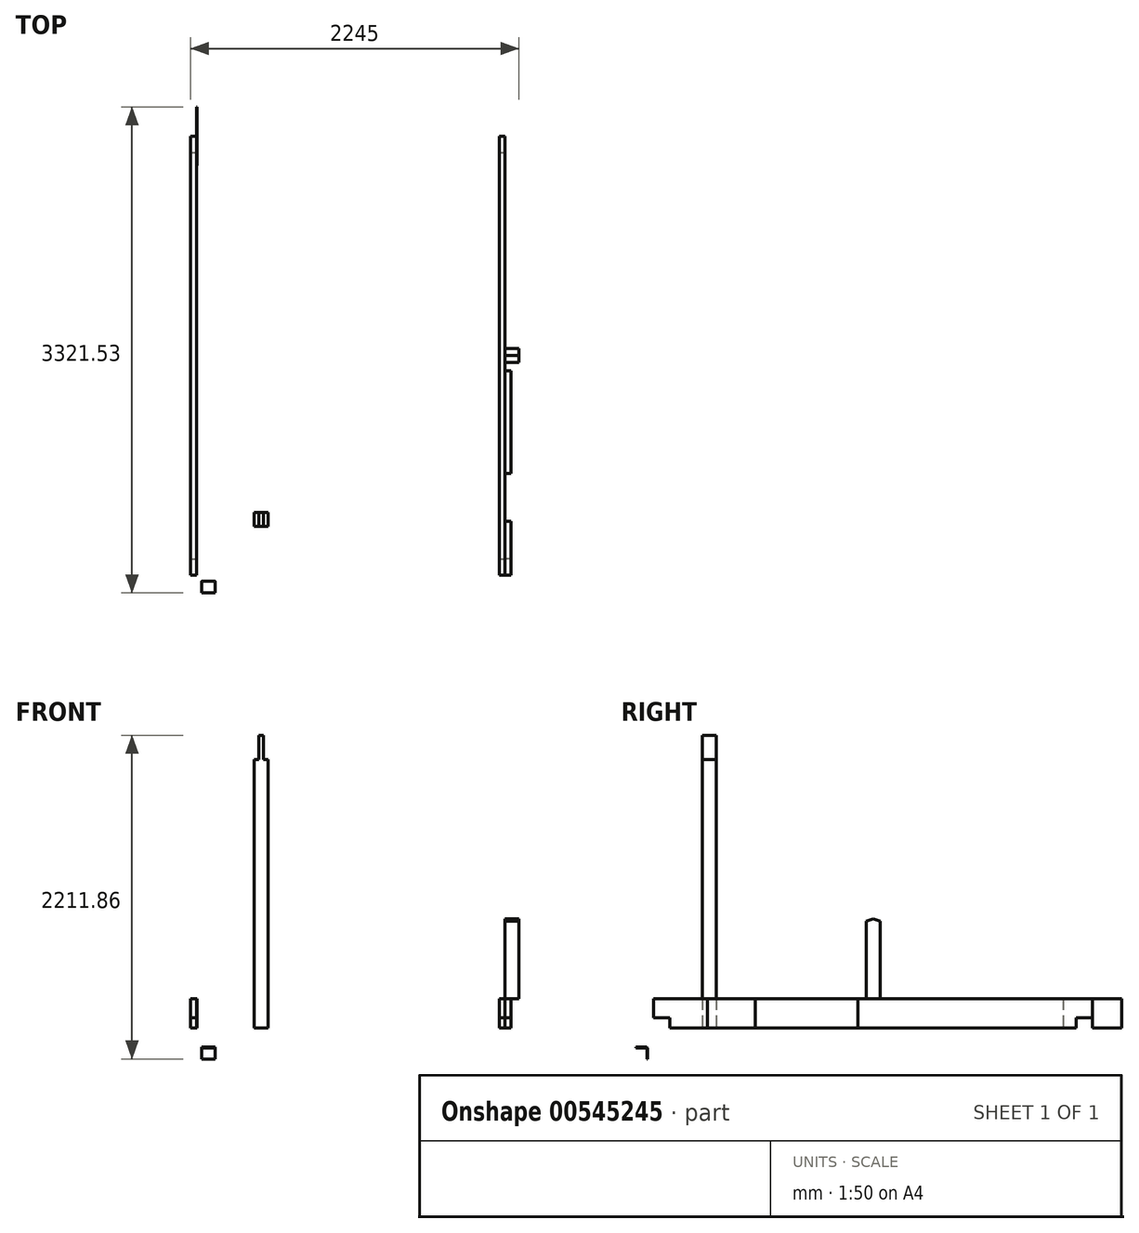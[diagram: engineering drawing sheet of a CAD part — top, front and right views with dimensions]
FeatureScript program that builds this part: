
annotation { "Feature Type Name" : "Feature", "Feature Type Description" : "" }
export const myFeature = defineFeature(function(context is Context, id is Id, definition is map)
    precondition{}
    {
        {
            assignVariable(context, id + "F0", {"name" : "dBalken", "anyValue" : 95});
        }
        {
            assignVariable(context, id + "F1", {"name" : "dBohle", "anyValue" : 40});
        }
        {
            var Q0;
            Q0=qCreatedBy(makeId("Top.planeOp"),FACE);
            var sketch = newSketch(context, id + "F2", { "sketchPlane" : qUnion([Q0])});
            skLineSegment(sketch, "E0.bottom", {"start": v(-76.6, 2841.51) * mm, "end": v(-36.6, 2841.51) * mm});
            skLineSegment(sketch, "E0.top", {"start": v(-76.6, -158.49) * mm, "end": v(-36.6, -158.49) * mm});
            skLineSegment(sketch, "E0.left", {"start": v(-76.6, 2841.51) * mm, "end": v(-76.6, -158.49) * mm});
            skLineSegment(sketch, "E0.right", {"start": v(-36.6, 2841.51) * mm, "end": v(-36.6, -158.49) * mm});
            skLineSegment(sketch, "E1.bottom", {"start": v(357.98, 268.38) * mm, "end": v(452.98, 268.38) * mm});
            skLineSegment(sketch, "E1.top", {"start": v(357.98, 173.38) * mm, "end": v(452.98, 173.38) * mm});
            skLineSegment(sketch, "E1.left", {"start": v(357.98, 268.38) * mm, "end": v(357.98, 173.38) * mm});
            skLineSegment(sketch, "E1.right", {"start": v(452.98, 268.38) * mm, "end": v(452.98, 173.38) * mm});
            skSolve(sketch);
        }
        {
            var Q0;
            Q0=makeQuery(id+"F2.imprint","IMPRINT",FACE,{"disambiguationData":[TD([[makeQuery(id+"F2.imprint","IMPRINT",EDGE,{"derivedFrom":sQuery(id+"F2.wireOp",EDGE,"E0.bottom")}),-1.0]])]});
            extrude(context, id + "F3", {"entities" : qUnion([Q0]), "depth" : 200 * mm, "offsetDistance" : 25 * mm});
        }
        {
            var Q0;
            Q0=makeQuery(id+"F2.imprint","IMPRINT",FACE,{"disambiguationData":[TD([[makeQuery(id+"F2.imprint","IMPRINT",EDGE,{"derivedFrom":sQuery(id+"F2.wireOp",EDGE,"E1.bottom")}),-1.0]])]});
            extrude(context, id + "F4", {"entities" : qUnion([Q0]), "depth" : 2000 * mm, "offsetDistance" : 25 * mm});
        }
        {
            var Q0;
            Q0=makeQuery(id+"F4.opExtrude","SWEPT_FACE",FACE,{"disambiguationData":[OSD([sQuery(id+"F2.wireOp",EDGE,"E1.top")])]});
            var sketch = newSketch(context, id + "F5", { "sketchPlane" : qUnion([Q0])});
            skLineSegment(sketch, "E2", {"start": v(405.48, 2000) * mm, "end": v(405.48, 2049.78) * mm, "construction": true});
            skLineSegment(sketch, "E3", {"start": v(389.98, 2000) * mm, "end": v(389.98, 1835.86) * mm});
            skLineSegment(sketch, "E4", {"start": v(389.98, 1835.86) * mm, "end": v(357.98, 1835.86) * mm});
            skLineSegment(sketch, "E5.MirrorCS", {"start": v(420.98, 2000) * mm, "end": v(420.98, 1835.86) * mm});
            skLineSegment(sketch, "E6.MirrorCS", {"start": v(420.98, 1835.86) * mm, "end": v(452.98, 1835.86) * mm});
            skSolve(sketch);
        }
        {
            var Q0;
            {var subQ0=sQuery(id+"F5.wireOp",EDGE,"E3");Q0=makeQuery(id+"F5.imprint","IMPRINT",FACE,{"disambiguationData":[TD([[makeQuery(id+"F5.imprint","IMPRINT",EDGE,{"derivedFrom":subQ0}),-1.0]])]});}
            var Q1;
            {var subQ0=sQuery(id+"F5.wireOp",EDGE,"E5.MirrorCS");Q1=makeQuery(id+"F5.imprint","IMPRINT",FACE,{"disambiguationData":[TD([[makeQuery(id+"F5.imprint","IMPRINT",EDGE,{"derivedFrom":subQ0}),1.0]])]});}
            extrude(context, id + "F6", {"entities" : qUnion([Q0, Q1]), "operationType" : NewBodyOperationType.REMOVE, "endBound" : BoundingType.THROUGH_ALL, "oppositeDirection" : true, "depth" : 25 * mm, "offsetDistance" : 25 * mm});
        }
        {
            var Q0;
            Q0=qCreatedBy(makeId("Right.planeOp"),FACE);
            var sketch = newSketch(context, id + "F7", { "sketchPlane" : qUnion([Q0])});
            skLineSegment(sketch, "E7", {"start": v(-280.02, -131.86) * mm, "end": v(-210.02, -131.86) * mm});
            skLineSegment(sketch, "E8", {"start": v(-200.02, -211.86) * mm, "end": v(-200.02, -141.86) * mm});
            skLineSegment(sketch, "E9.0", {"start": v(-205.02, -211.86) * mm, "end": v(-205.02, -141.86) * mm});
            skLineSegment(sketch, "E9.1", {"start": v(-280.02, -136.86) * mm, "end": v(-210.02, -136.86) * mm});
            skLineSegment(sketch, "E10", {"start": v(-280.02, -131.86) * mm, "end": v(-280.02, -136.86) * mm});
            skLineSegment(sketch, "E11", {"start": v(-205.02, -211.86) * mm, "end": v(-200.02, -211.86) * mm});
            skPoint(sketch, "E12.visualSharp", {"position": v(-205.02, -136.86) * mm});
            skArc(sketch, "E12.filletArc", {"start": v(-205.02, -141.86) * mm, "mid": v(-206.48, -138.32) * mm, "end": v(-210.02, -136.86) * mm});
            skPoint(sketch, "E13.visualSharp", {"position": v(-200.02, -131.86) * mm});
            skArc(sketch, "E13.filletArc", {"start": v(-200.02, -141.86) * mm, "mid": v(-202.95, -134.78) * mm, "end": v(-210.02, -131.86) * mm});
            skSolve(sketch);
        }
        {
            var Q0;
            Q0=makeQuery(id+"F7.imprint","IMPRINT",FACE,{"disambiguationData":[TD([[makeQuery(id+"F7.imprint","IMPRINT",EDGE,{"derivedFrom":sQuery(id+"F7.wireOp",EDGE,"E7")}),-1.0]])]});
            extrude(context, id + "F8", {"entities" : qUnion([Q0]), "depth" : 90 * mm, "offsetDistance" : 25 * mm});
        }
        {
            var Q0;
            Q0=makeQuery(id+"F3.opExtrude","SWEPT_FACE",FACE,{"disambiguationData":[OSD([sQuery(id+"F2.wireOp",EDGE,"E0.right")])]});
            var sketch = newSketch(context, id + "F9", { "sketchPlane" : qUnion([Q0])});
            skLineSegment(sketch, "E14.0", {"start": v(2841.51, 200) * mm, "end": v(-158.49, 200) * mm, "construction": true});
            skLineSegment(sketch, "E15.0", {"start": v(2841.51, 200) * mm, "end": v(2841.51, 0) * mm, "construction": true});
            skLineSegment(sketch, "E16.0", {"start": v(2841.51, 0) * mm, "end": v(-158.49, 0) * mm, "construction": true});
            skLineSegment(sketch, "E17.bottom", {"start": v(2641.51, 200) * mm, "end": v(2841.51, 200) * mm});
            skLineSegment(sketch, "E17.top", {"start": v(2641.51, 0) * mm, "end": v(2841.51, 0) * mm});
            skLineSegment(sketch, "E17.left", {"start": v(2641.51, 200) * mm, "end": v(2641.51, 0) * mm});
            skLineSegment(sketch, "E17.right", {"start": v(3041.51, 200) * mm, "end": v(3041.51, 0) * mm});
            skLineSegment(sketch, "E18", {"start": v(2841.51, 200) * mm, "end": v(3041.51, 200) * mm});
            skLineSegment(sketch, "E19", {"start": v(2841.51, 0) * mm, "end": v(3041.51, 0) * mm});
            skSolve(sketch);
        }
        {
            var Q0;
            Q0=makeQuery(id+"F9.imprint","IMPRINT",FACE,{"disambiguationData":[TD([[makeQuery(id+"F9.imprint","IMPRINT",EDGE,{"derivedFrom":sQuery(id+"F9.wireOp",EDGE,"E17.bottom")}),1.0]])]});
            var Q1;
            Q1=makeQuery(id+"F9.imprint","IMPRINT",FACE,{"disambiguationData":[TD([[makeQuery(id+"F9.imprint","IMPRINT",EDGE,{"derivedFrom":sQuery(id+"F9.wireOp",EDGE,"E17.right")}),-1.0]])]});
            extrude(context, id + "F10", {"entities" : qUnion([Q0, Q1]), "depth" : 4 * mm, "offsetDistance" : 25 * mm});
        }
        {
            var Q0;
            Q0=makeQuery(id+"F3.opExtrude","SWEPT_BODY",BODY,{"disambiguationData":[OSD([sQuery(id+"F2.wireOp",EDGE,"E0.bottom"),sQuery(id+"F2.wireOp",EDGE,"E0.top"),sQuery(id+"F2.wireOp",EDGE,"E0.left"),sQuery(id+"F2.wireOp",EDGE,"E0.right")])]});
            transform(context, id + "F11", {"entities" : qUnion([Q0]), "transformType" : TransformType.TRANSLATION_3D, "dx" : 2110 * mm, "dy" : 0 * mm, "dz" : 0 * mm, "makeCopy" : true});
        }
        {
            var Q0;
            Q0=makeQuery(id+"F11.opPattern","COPY",FACE,{"derivedFrom":makeQuery(id+"F3.opExtrude","SWEPT_FACE",FACE,{"disambiguationData":[OSD([sQuery(id+"F2.wireOp",EDGE,"E0.right")])]}),"instanceName":"1"});
            var sketch = newSketch(context, id + "F12", { "sketchPlane" : qUnion([Q0])});
            skLineSegment(sketch, "E20.0", {"start": v(-158.49, 200) * mm, "end": v(-158.49, 0) * mm});
            skLineSegment(sketch, "E21.0", {"start": v(2841.51, 0) * mm, "end": v(-158.49, 0) * mm});
            skLineSegment(sketch, "E22.0", {"start": v(2841.51, 200) * mm, "end": v(-158.49, 200) * mm});
            skLineSegment(sketch, "E23", {"start": v(1341.51, 200) * mm, "end": v(1341.51, 496.67) * mm, "construction": true});
            skPoint(sketch, "E23.endSnap0", {"position": v(1341.51, 200) * mm});
            skLineSegment(sketch, "E24", {"start": v(-158.49, 70) * mm, "end": v(-47.49, 70) * mm});
            skLineSegment(sketch, "E25", {"start": v(-47.49, 70) * mm, "end": v(-47.49, 0) * mm});
            skLineSegment(sketch, "E26.MirrorCS", {"start": v(2730.51, 70) * mm, "end": v(2730.51, 0) * mm});
            skLineSegment(sketch, "E27.MirrorCS", {"start": v(2841.51, 70) * mm, "end": v(2730.51, 70) * mm});
            skLineSegment(sketch, "E28", {"start": v(-707.98, 0) * mm, "end": v(1294.01, 728.67) * mm});
            skLineSegment(sketch, "E29", {"start": v(1294.01, 0) * mm, "end": v(1294.01, 728.67) * mm});
            skLineSegment(sketch, "E30.MirrorCS", {"start": v(1389.01, 0) * mm, "end": v(1389.01, 728.67) * mm});
            skLineSegment(sketch, "E31", {"start": v(1294.01, 728.67) * mm, "end": v(1341.51, 745.96) * mm});
            skLineSegment(sketch, "E32", {"start": v(1389.01, 728.67) * mm, "end": v(1341.51, 745.96) * mm});
            skSolve(sketch);
        }
        {
            var Q0;
            {var subQ3=sQuery(id+"F12.wireOp",EDGE,"E24");Q0=makeQuery(id+"F12.imprint","IMPRINT",FACE,{"disambiguationData":[TD([[makeQuery(id+"F12.imprint","IMPRINT",EDGE,{"derivedFrom":subQ3}),-1.0]])]});}
            var Q1;
            {var subQ3=sQuery(id+"F12.wireOp",EDGE,"E26.MirrorCS");Q1=makeQuery(id+"F12.imprint","IMPRINT",FACE,{"disambiguationData":[TD([[makeQuery(id+"F12.imprint","IMPRINT",EDGE,{"derivedFrom":subQ3}),1.0]])]});}
            extrude(context, id + "F13", {"entities" : qUnion([Q0, Q1]), "operationType" : NewBodyOperationType.REMOVE, "endBound" : BoundingType.THROUGH_ALL, "oppositeDirection" : true, "depth" : 25 * mm, "offsetDistance" : 25 * mm});
        }
        {
            var Q0;
            Q0=makeQuery(id+"F11.opPattern","COPY",FACE,{"derivedFrom":makeQuery(id+"F3.opExtrude","SWEPT_FACE",FACE,{"disambiguationData":[OSD([sQuery(id+"F2.wireOp",EDGE,"E0.right")])]}),"instanceName":"1"});
            var sketch = newSketch(context, id + "F14", { "sketchPlane" : qUnion([Q0])});
            skLineSegment(sketch, "E33.0", {"start": v(2841.51, 200) * mm, "end": v(-158.49, 200) * mm, "construction": true});
            skLineSegment(sketch, "E34.0", {"start": v(2730.51, 0) * mm, "end": v(-47.49, 0) * mm, "construction": true});
            skPoint(sketch, "E35.0", {"position": v(-158.49, 135) * mm});
            skLineSegment(sketch, "E36.0", {"start": v(-158.49, 200) * mm, "end": v(-158.49, 70) * mm, "construction": true});
            skLineSegment(sketch, "E37.0", {"start": v(-158.49, 70) * mm, "end": v(-47.49, 70) * mm, "construction": true});
            skLineSegment(sketch, "E38.0", {"start": v(-47.49, 70) * mm, "end": v(-47.49, 0) * mm, "construction": true});
            skLineSegment(sketch, "E39", {"start": v(-158.49, 200) * mm, "end": v(209.7, 200) * mm});
            skLineSegment(sketch, "E40", {"start": v(209.7, 200) * mm, "end": v(209.7, 0) * mm});
            skLineSegment(sketch, "E41", {"start": v(209.7, 0) * mm, "end": v(-47.49, 0) * mm});
            skLineSegment(sketch, "E42", {"start": v(-47.49, 70) * mm, "end": v(-158.49, 70) * mm});
            skLineSegment(sketch, "E43", {"start": v(-158.49, 186.48) * mm, "end": v(-158.49, 200) * mm});
            skLineSegment(sketch, "E44", {"start": v(-158.49, 186.48) * mm, "end": v(-158.49, 70) * mm});
            skLineSegment(sketch, "E45.bottom", {"start": v(536.64, 0) * mm, "end": v(1236.64, 0) * mm});
            skLineSegment(sketch, "E45.top", {"start": v(536.64, 200) * mm, "end": v(1236.64, 200) * mm});
            skLineSegment(sketch, "E45.left", {"start": v(536.64, 0) * mm, "end": v(536.64, 200) * mm});
            skLineSegment(sketch, "E45.right", {"start": v(1236.64, 0) * mm, "end": v(1236.64, 200) * mm});
            skSolve(sketch);
        }
        {
            var Q0;
            Q0=makeQuery(id+"F14.imprint","IMPRINT",FACE,{"disambiguationData":[TD([[makeQuery(id+"F14.imprint","IMPRINT",EDGE,{"derivedFrom":sQuery(id+"F14.wireOp",EDGE,"E39")}),1.0]])]});
            var Q1;
            Q1=makeQuery(id+"F14.imprint","IMPRINT",FACE,{"disambiguationData":[TD([[makeQuery(id+"F14.imprint","IMPRINT",EDGE,{"derivedFrom":sQuery(id+"F14.wireOp",EDGE,"E45.bottom")}),-1.0]])]});
            extrude(context, id + "F15", {"entities" : qUnion([Q0, Q1]), "depth" : (getVariable(context, 'dBohle')) * mm, "offsetDistance" : 25 * mm});
        }
        {
            var Q0;
            {var subQ0=sQuery(id+"F12.wireOp",EDGE,"E31");Q0=makeQuery(id+"F12.imprint","IMPRINT",FACE,{"disambiguationData":[TD([[makeQuery(id+"F12.imprint","IMPRINT",EDGE,{"derivedFrom":subQ0}),-1.0]])]});}
            extrude(context, id + "F16", {"entities" : qUnion([Q0]), "depth" : (getVariable(context, 'dBalken')) * mm, "offsetDistance" : 25 * mm});
        }
    });
